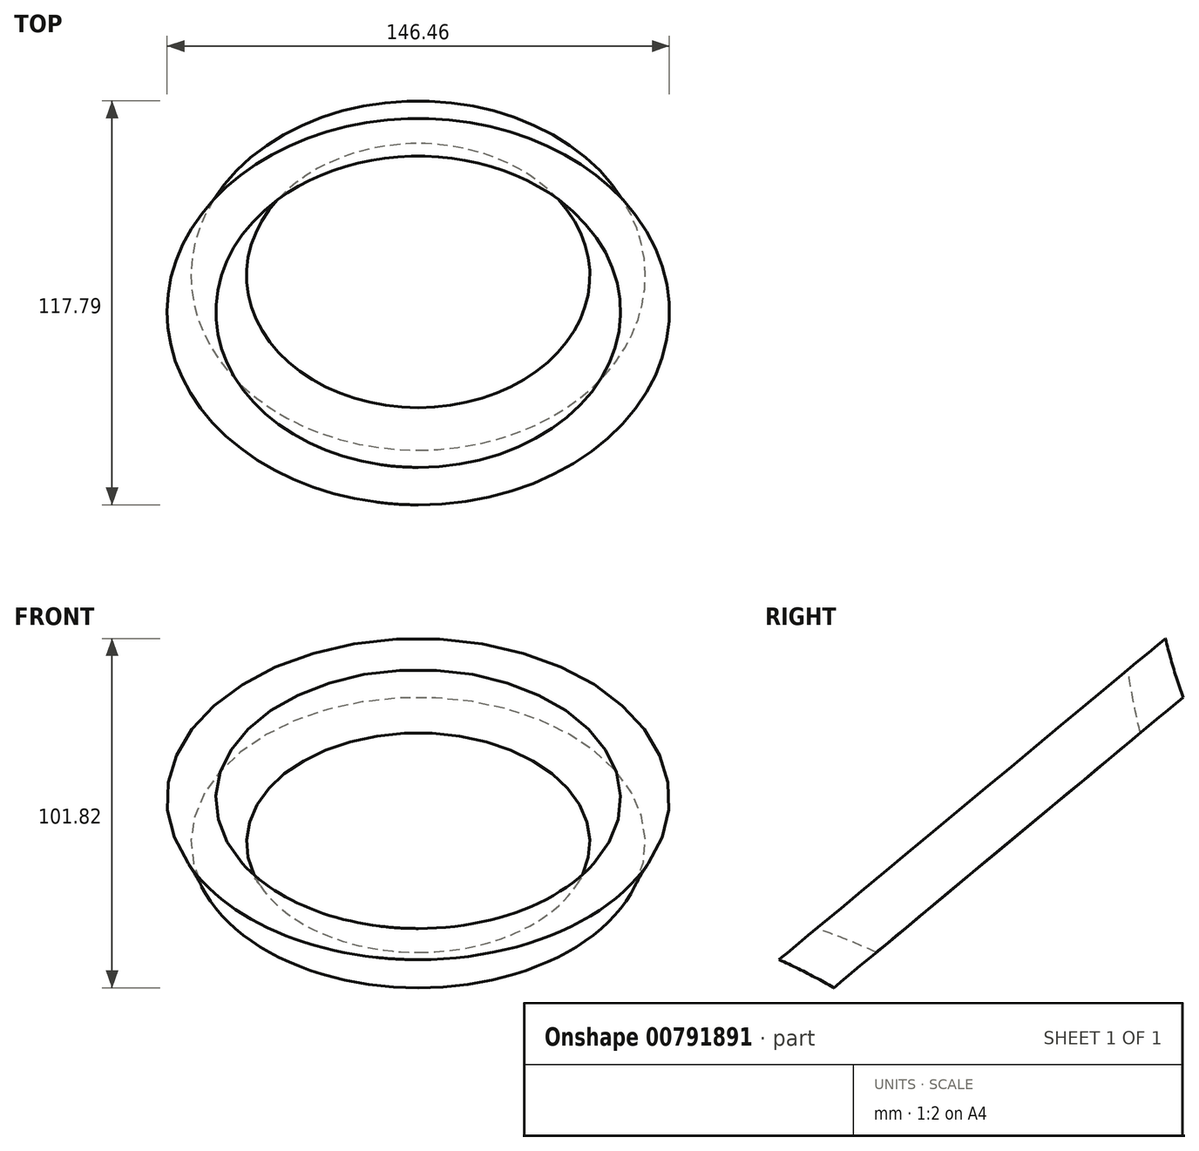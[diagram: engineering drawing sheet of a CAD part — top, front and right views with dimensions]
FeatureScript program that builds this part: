
annotation { "Feature Type Name" : "Feature", "Feature Type Description" : "" }
export const myFeature = defineFeature(function(context is Context, id is Id, definition is map)
    precondition{}
    {
        {
            var Q0;
            Q0=qCreatedBy(makeId("Front.planeOp"),FACE);
            var sketch = newSketch(context, id + "F0", { "sketchPlane" : qUnion([Q0])});
            skLineSegment(sketch, "E0.bottom", {"start": v(-59.65, 50.57) * mm, "end": v(-40.96, 50.57) * mm});
            skLineSegment(sketch, "E0.top", {"start": v(-59.65, 29.14) * mm, "end": v(-40.96, 29.14) * mm});
            skLineSegment(sketch, "E0.left", {"start": v(-59.65, 50.57) * mm, "end": v(-59.65, 29.14) * mm});
            skLineSegment(sketch, "E0.right", {"start": v(-40.96, 50.57) * mm, "end": v(-40.96, 29.14) * mm});
            skLineSegment(sketch, "E1", {"start": v(0, 0) * mm, "end": v(-60.6, 0) * mm});
            skLineSegment(sketch, "E2", {"start": v(0, 0) * mm, "end": v(-59.64, -17.92) * mm});
            skLineSegment(sketch, "E3", {"start": v(-59.64, -17.92) * mm, "end": v(-65.98, -18.03) * mm});
            skSolve(sketch);
        }
        {
            var Q0;
            Q0=qCreatedBy(makeId("Right.planeOp"),FACE);
            var sketch = newSketch(context, id + "F1", { "sketchPlane" : qUnion([Q0])});
            skLineSegment(sketch, "E4", {"start": v(-67.44, 67.4) * mm, "end": v(-39, 55.83) * mm});
            skLineSegment(sketch, "E5", {"start": v(-39, 55.83) * mm, "end": v(-59.62, 55.83) * mm});
            skLineSegment(sketch, "E6", {"start": v(-59.62, 55.83) * mm, "end": v(21.4, -41.63) * mm});
            skSolve(sketch);
        }
        {
            var Q0;
            Q0=makeQuery(id+"F0.imprint","IMPRINT",FACE,{"disambiguationData":[TD([[makeQuery(id+"F0.imprint","IMPRINT",EDGE,{"derivedFrom":sQuery(id+"F0.wireOp",EDGE,"E0.bottom")}),-1.0]])]});
            var Q1;
            Q1=sQuery(id+"F1.wireOp",EDGE,"E6");
            revolve(context, id + "F2", {"surfaceOperationType" : NewSurfaceOperationType.NEW, "entities" : qUnion([Q0]), "axis" : qUnion([Q1]), "revolveType" : RevolveType.FULL});
        }
    });
